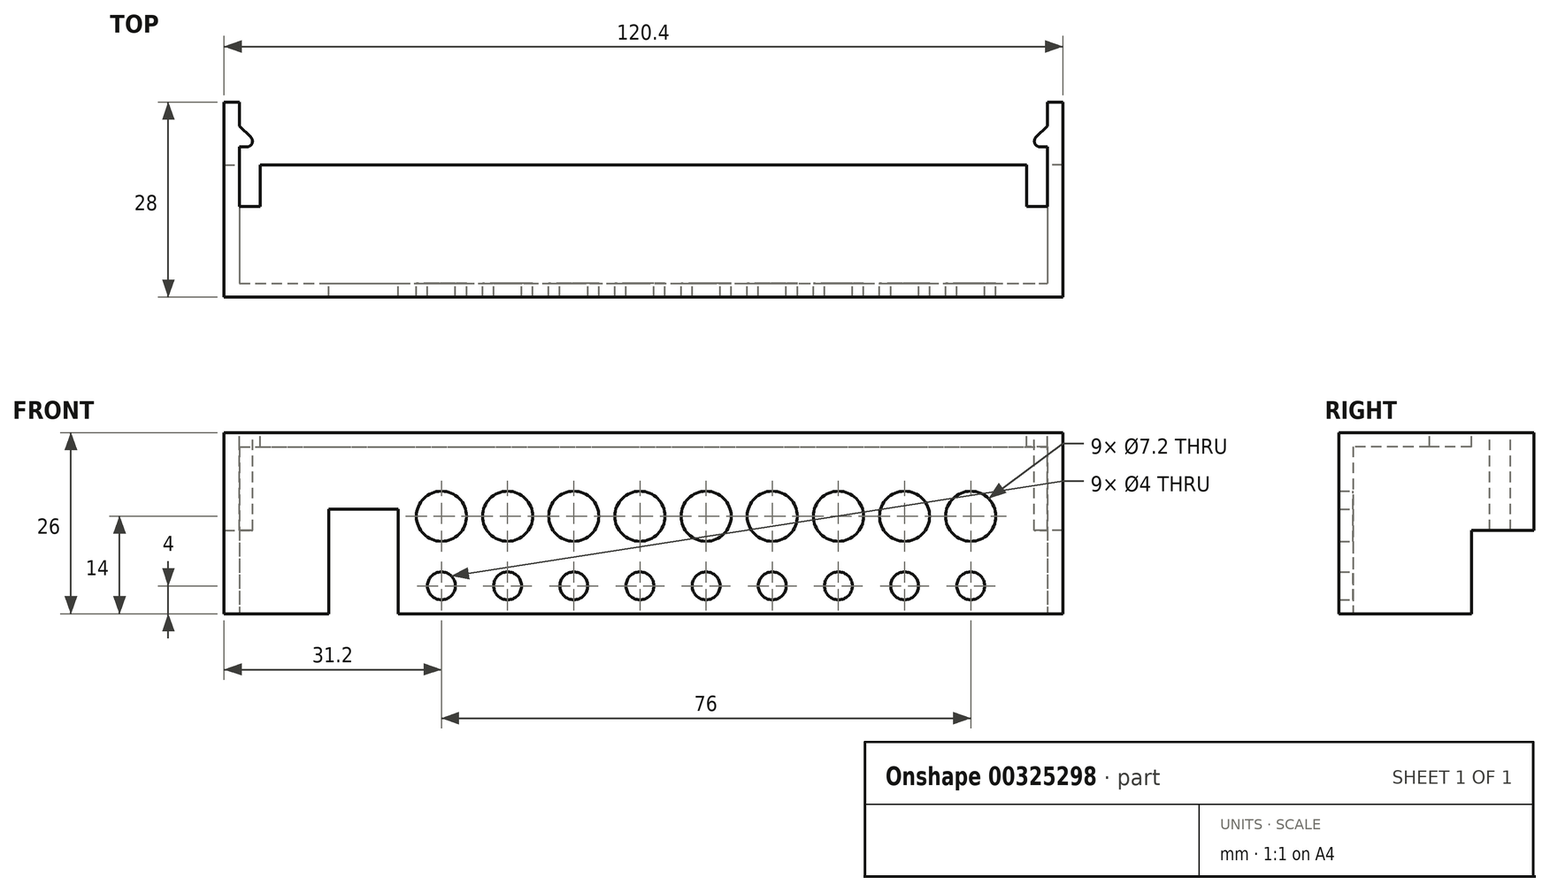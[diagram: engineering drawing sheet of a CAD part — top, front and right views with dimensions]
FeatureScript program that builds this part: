
annotation { "Feature Type Name" : "Feature", "Feature Type Description" : "" }
export const myFeature = defineFeature(function(context is Context, id is Id, definition is map)
    precondition{}
    {
        {
            var Q0;
            Q0=qCreatedBy(makeId("Top.planeOp"),FACE);
            var sketch = newSketch(context, id + "F0", { "sketchPlane" : qUnion([Q0])});
            skLineSegment(sketch, "E0.bottom", {"start": v(-58, 17) * mm, "end": v(58, 17) * mm});
            skLineSegment(sketch, "E0.top", {"start": v(-58, 0) * mm, "end": v(58, 0) * mm});
            skLineSegment(sketch, "E0.left", {"start": v(-58, 17) * mm, "end": v(-58, 0) * mm});
            skLineSegment(sketch, "E0.right", {"start": v(58, 17) * mm, "end": v(58, 0) * mm});
            skSolve(sketch);
        }
        {
            var Q0;
            Q0=makeQuery(id+"F0.imprint","IMPRINT",FACE,{"disambiguationData":[TD([[makeQuery(id+"F0.imprint","IMPRINT",EDGE,{"derivedFrom":sQuery(id+"F0.wireOp",EDGE,"E0.bottom")}),-1.0]])]});
            extrude(context, id + "F1", {"entities" : qUnion([Q0]), "depth" : 2 * mm});
        }
        {
            var Q0;
            Q0=makeQuery(id+"F1.opExtrude","SWEPT_FACE",FACE,{"disambiguationData":[OSD([sQuery(id+"F0.wireOp",EDGE,"E0.left")])]});
            var sketch = newSketch(context, id + "F2", { "sketchPlane" : qUnion([Q0])});
            skLineSegment(sketch, "E1.bottom", {"start": v(-17, 2) * mm, "end": v(0, 2) * mm});
            skLineSegment(sketch, "E1.top", {"start": v(-17, -24) * mm, "end": v(0, -24) * mm});
            skLineSegment(sketch, "E1.left", {"start": v(-17, 2) * mm, "end": v(-17, -24) * mm});
            skLineSegment(sketch, "E1.right", {"start": v(0, 2) * mm, "end": v(0, -24) * mm});
            skLineSegment(sketch, "E2.bottom", {"start": v(-17, -12) * mm, "end": v(-26, -12) * mm});
            skLineSegment(sketch, "E2.top", {"start": v(-17, 2) * mm, "end": v(-26, 2) * mm});
            skLineSegment(sketch, "E2.left", {"start": v(-17, -12) * mm, "end": v(-17, 2) * mm});
            skLineSegment(sketch, "E2.right", {"start": v(-26, -12) * mm, "end": v(-26, 2) * mm});
            skSolve(sketch);
        }
        {
            var Q0;
            {var subQ3=sQuery(id+"F2.wireOp",EDGE,"E2.bottom");Q0=makeQuery(id+"F2.imprint","IMPRINT",FACE,{"disambiguationData":[TD([[makeQuery(id+"F2.imprint","IMPRINT",EDGE,{"derivedFrom":subQ3}),-1.0]])]});}
            var Q1;
            {var subQ0=sQuery(id+"F2.wireOp",EDGE,"E1.bottom");Q1=makeQuery(id+"F2.imprint","IMPRINT",FACE,{"disambiguationData":[TD([[makeQuery(id+"F2.imprint","IMPRINT",EDGE,{"derivedFrom":subQ0}),-1.0]])]});}
            var Q2;
            {var subQ2=sQuery(id+"F2.wireOp",EDGE,"E1.top");Q2=makeQuery(id+"F2.imprint","IMPRINT",FACE,{"disambiguationData":[TD([[makeQuery(id+"F2.imprint","IMPRINT",EDGE,{"derivedFrom":subQ2}),1.0]])]});}
            extrude(context, id + "F3", {"entities" : qUnion([Q0, Q1, Q2]), "depth" : 2.2 * mm});
        }
        {
            var Q0;
            Q0=makeQuery(id+"F3.opExtrude","SWEPT_BODY",BODY,{"disambiguationData":[OSD([sQuery(id+"F2.wireOp",EDGE,"E1.bottom"),sQuery(id+"F2.wireOp",EDGE,"E1.top"),sQuery(id+"F2.wireOp",EDGE,"E1.left"),sQuery(id+"F2.wireOp",EDGE,"E1.right"),sQuery(id+"F2.wireOp",EDGE,"E2.bottom"),sQuery(id+"F2.wireOp",EDGE,"E2.top"),sQuery(id+"F2.wireOp",EDGE,"E2.right")])]});
            var Q1;
            Q1=qCreatedBy(makeId("Right.planeOp"),FACE);
            mirror(context, id + "F4", {"operationType" : NewBodyOperationType.ADD, "entities" : qUnion([Q0]), "mirrorPlane" : qUnion([Q1])});
        }
        {
            var Q0;
            {var subQ0=makeQuery(id+"F3.opExtrude","SWEPT_FACE",FACE,{"disambiguationData":[OSD([sQuery(id+"F2.wireOp",EDGE,"E1.bottom"),sQuery(id+"F2.wireOp",EDGE,"E2.top")])]});Q0=makeQuery(id+"F4.boolean.opBoolean","MERGE",FACE,{"derivedFrom":[makeQuery(id+"F1.opExtrude","CAP_FACE",FACE,{"disambiguationData":[OSD([sQuery(id+"F0.wireOp",EDGE,"E0.bottom"),sQuery(id+"F0.wireOp",EDGE,"E0.top"),sQuery(id+"F0.wireOp",EDGE,"E0.left"),sQuery(id+"F0.wireOp",EDGE,"E0.right")])],"isStart":false}),subQ0,makeQuery(id+"F4.opPattern","COPY",FACE,{"derivedFrom":subQ0,"instanceName":"1"})]});}
            var sketch = newSketch(context, id + "F5", { "sketchPlane" : qUnion([Q0])});
            skLineSegment(sketch, "E3.bottom", {"start": v(-58, 17) * mm, "end": v(-55, 17) * mm});
            skLineSegment(sketch, "E3.top", {"start": v(-58, 11) * mm, "end": v(-55, 11) * mm});
            skLineSegment(sketch, "E3.left", {"start": v(-58, 17) * mm, "end": v(-58, 11) * mm});
            skLineSegment(sketch, "E3.right", {"start": v(-55, 17) * mm, "end": v(-55, 11) * mm});
            skLineSegment(sketch, "E4.MirrorCS", {"start": v(58, 17) * mm, "end": v(55, 17) * mm});
            skLineSegment(sketch, "E5.MirrorCS", {"start": v(58, 17) * mm, "end": v(58, 11) * mm});
            skLineSegment(sketch, "E6.MirrorCS", {"start": v(58, 11) * mm, "end": v(55, 11) * mm});
            skLineSegment(sketch, "E7.MirrorCS", {"start": v(55, 17) * mm, "end": v(55, 11) * mm});
            skSolve(sketch);
        }
        {
            var Q0;
            Q0=makeQuery(id+"F5.imprint","IMPRINT",FACE,{"disambiguationData":[TD([[makeQuery(id+"F5.imprint","IMPRINT",EDGE,{"derivedFrom":sQuery(id+"F5.wireOp",EDGE,"E3.bottom")}),-1.0]])]});
            var Q1;
            Q1=makeQuery(id+"F5.imprint","IMPRINT",FACE,{"disambiguationData":[TD([[makeQuery(id+"F5.imprint","IMPRINT",EDGE,{"derivedFrom":sQuery(id+"F5.wireOp",EDGE,"E4.MirrorCS")}),-1.0]])]});
            extrude(context, id + "F6", {"entities" : qUnion([Q0, Q1]), "operationType" : NewBodyOperationType.REMOVE, "oppositeDirection" : true, "depth" : 25 * mm});
        }
        {
            var Q0;
            {var subQ0=makeQuery(id+"F3.opExtrude","SWEPT_FACE",FACE,{"disambiguationData":[OSD([sQuery(id+"F2.wireOp",EDGE,"E1.bottom"),sQuery(id+"F2.wireOp",EDGE,"E2.top")])]});Q0=makeQuery(id+"F4.boolean.opBoolean","MERGE",FACE,{"derivedFrom":[makeQuery(id+"F1.opExtrude","CAP_FACE",FACE,{"disambiguationData":[OSD([sQuery(id+"F0.wireOp",EDGE,"E0.bottom"),sQuery(id+"F0.wireOp",EDGE,"E0.top"),sQuery(id+"F0.wireOp",EDGE,"E0.left"),sQuery(id+"F0.wireOp",EDGE,"E0.right")])],"isStart":false}),subQ0,makeQuery(id+"F4.opPattern","COPY",FACE,{"derivedFrom":subQ0,"instanceName":"1"})]});}
            var sketch = newSketch(context, id + "F7", { "sketchPlane" : qUnion([Q0])});
            skLineSegment(sketch, "E8", {"start": v(-58, 22.6) * mm, "end": v(-55, 19.6) * mm});
            skLineSegment(sketch, "E9", {"start": v(-55, 19.6) * mm, "end": v(-58, 19.6) * mm});
            skLineSegment(sketch, "E10.0", {"start": v(-58, 11) * mm, "end": v(-58, 26) * mm});
            skLineSegment(sketch, "E11.MirrorCS", {"start": v(55, 19.6) * mm, "end": v(58, 19.6) * mm});
            skLineSegment(sketch, "E12.MirrorCS", {"start": v(58, 22.6) * mm, "end": v(55, 19.6) * mm});
            skLineSegment(sketch, "E13.MirrorCS", {"start": v(58, 11) * mm, "end": v(58, 26) * mm});
            skSolve(sketch);
        }
        {
            var Q0;
            {var subQ0=sQuery(id+"F7.wireOp",EDGE,"E8");Q0=makeQuery(id+"F7.imprint","IMPRINT",FACE,{"disambiguationData":[TD([[makeQuery(id+"F7.imprint","IMPRINT",EDGE,{"derivedFrom":subQ0}),-1.0]])]});}
            var Q1;
            {var subQ0=sQuery(id+"F7.wireOp",EDGE,"E11.MirrorCS");Q1=makeQuery(id+"F7.imprint","IMPRINT",FACE,{"disambiguationData":[TD([[makeQuery(id+"F7.imprint","IMPRINT",EDGE,{"derivedFrom":subQ0}),1.0]])]});}
            var Q2;
            Q2=makeQuery(id+"F3.opExtrude","SWEPT_FACE",FACE,{"disambiguationData":[OSD([sQuery(id+"F2.wireOp",EDGE,"E2.bottom")])]});
            extrude(context, id + "F8", {"entities" : qUnion([Q0, Q1]), "operationType" : NewBodyOperationType.ADD, "endBound" : BoundingType.UP_TO_SURFACE, "oppositeDirection" : true, "endBoundEntityFace" : qUnion([Q2]), "depth" : 25 * mm});
        }
        {
            var Q0;
            Q0=makeQuery(id+"F8.opExtrude","SWEPT_EDGE",EDGE,{"disambiguationData":[OSD([sQuery(id+"F7.wireOp",EDGE,"E11.MirrorCS"),sQuery(id+"F7.wireOp",EDGE,"E12.MirrorCS")])]});
            var Q1;
            Q1=makeQuery(id+"F8.opExtrude","SWEPT_EDGE",EDGE,{"disambiguationData":[OSD([sQuery(id+"F7.wireOp",EDGE,"E8"),sQuery(id+"F7.wireOp",EDGE,"E9")])]});
            var Q2;
            Q2=makeQuery(id+"F8.opExtrude","SWEPT_EDGE",EDGE,{"disambiguationData":[OSD([sQuery(id+"F7.wireOp",EDGE,"E11.MirrorCS"),sQuery(id+"F7.wireOp",EDGE,"E13.MirrorCS")])]});
            var Q3;
            Q3=makeQuery(id+"F8.opExtrude","SWEPT_EDGE",EDGE,{"disambiguationData":[OSD([sQuery(id+"F7.wireOp",EDGE,"E9"),sQuery(id+"F7.wireOp",EDGE,"E10.0")])]});
            var Q4;
            Q4=makeQuery(id+"F8.opExtrude","SWEPT_EDGE",EDGE,{"disambiguationData":[OSD([sQuery(id+"F7.wireOp",EDGE,"E8"),sQuery(id+"F7.wireOp",EDGE,"E10.0")])]});
            var Q5;
            Q5=makeQuery(id+"F8.opExtrude","SWEPT_EDGE",EDGE,{"disambiguationData":[OSD([sQuery(id+"F7.wireOp",EDGE,"E12.MirrorCS"),sQuery(id+"F7.wireOp",EDGE,"E13.MirrorCS")])]});
            fillet(context, id + "F9", {"entities" : qUnion([Q0, Q1, Q2, Q3, Q4, Q5]), "radius" : .8 * mm, "tangentPropagation" : true, "allowEdgeOverflow" : false});
        }
        {
            var Q0;
            {var subQ0=makeQuery(id+"F3.opExtrude","SWEPT_FACE",FACE,{"disambiguationData":[OSD([sQuery(id+"F2.wireOp",EDGE,"E1.right")])]});Q0=makeQuery(id+"F4.boolean.opBoolean","MERGE",FACE,{"derivedFrom":[makeQuery(id+"F1.opExtrude","SWEPT_FACE",FACE,{"disambiguationData":[OSD([sQuery(id+"F0.wireOp",EDGE,"E0.top")])]}),subQ0,makeQuery(id+"F4.opPattern","COPY",FACE,{"derivedFrom":subQ0,"instanceName":"1"})]});}
            var sketch = newSketch(context, id + "F10", { "sketchPlane" : qUnion([Q0])});
            skLineSegment(sketch, "E14.0", {"start": v(-60.2, 2) * mm, "end": v(-60.2, -24) * mm});
            skLineSegment(sketch, "E15.0", {"start": v(-60.2, 2) * mm, "end": v(60.2, 2) * mm});
            skLineSegment(sketch, "E16.0", {"start": v(60.2, 2) * mm, "end": v(60.2, -24) * mm});
            skLineSegment(sketch, "E17", {"start": v(-60.2, -24) * mm, "end": v(-45.2, -24) * mm});
            skLineSegment(sketch, "E18", {"start": v(-45.2, -24) * mm, "end": v(-45.2, -9) * mm});
            skLineSegment(sketch, "E19", {"start": v(-45.2, -9) * mm, "end": v(-35.2, -9) * mm});
            skLineSegment(sketch, "E20", {"start": v(-35.2, -9) * mm, "end": v(-35.2, -24) * mm});
            skLineSegment(sketch, "E21", {"start": v(-35.2, -24) * mm, "end": v(60.2, -24) * mm});
            skCircle(sketch, "E22", {"center": v(-29, -20) * mm, "radius": 2 * mm});
            skCircle(sketch, "E23", {"center": v(-29, -10) * mm, "radius": 3.6 * mm});
            skCircle(sketch, "E24.1.0.0", {"center": v(-19.5, -10) * mm, "radius": 3.6 * mm});
            skCircle(sketch, "E24.1.0.1", {"center": v(-19.5, -20) * mm, "radius": 2 * mm});
            skCircle(sketch, "E24.2.0.0", {"center": v(-10, -10) * mm, "radius": 3.6 * mm});
            skCircle(sketch, "E24.2.0.1", {"center": v(-10, -20) * mm, "radius": 2 * mm});
            skCircle(sketch, "E24.3.0.0", {"center": v(-0.5, -10) * mm, "radius": 3.6 * mm});
            skCircle(sketch, "E24.3.0.1", {"center": v(-0.5, -20) * mm, "radius": 2 * mm});
            skCircle(sketch, "E24.4.0.0", {"center": v(9, -10) * mm, "radius": 3.6 * mm});
            skCircle(sketch, "E24.4.0.1", {"center": v(9, -20) * mm, "radius": 2 * mm});
            skCircle(sketch, "E24.5.0.0", {"center": v(18.5, -10) * mm, "radius": 3.6 * mm});
            skCircle(sketch, "E24.5.0.1", {"center": v(18.5, -20) * mm, "radius": 2 * mm});
            skCircle(sketch, "E24.6.0.0", {"center": v(28, -10) * mm, "radius": 3.6 * mm});
            skCircle(sketch, "E24.6.0.1", {"center": v(28, -20) * mm, "radius": 2 * mm});
            skCircle(sketch, "E24.7.0.0", {"center": v(37.5, -10) * mm, "radius": 3.6 * mm});
            skCircle(sketch, "E24.7.0.1", {"center": v(37.5, -20) * mm, "radius": 2 * mm});
            skCircle(sketch, "E24.8.0.0", {"center": v(47, -10) * mm, "radius": 3.6 * mm});
            skCircle(sketch, "E24.8.0.1", {"center": v(47, -20) * mm, "radius": 2 * mm});
            skLineSegment(sketch, "E24.direction1", {"start": v(-29, -10) * mm, "end": v(-19.5, -10) * mm, "construction": true});
            skSolve(sketch);
        }
        {
            var Q0;
            {var subQ1=sQuery(id+"F10.wireOp",EDGE,"E18");Q0=makeQuery(id+"F10.imprint","IMPRINT",FACE,{"disambiguationData":[TD([[makeQuery(id+"F10.imprint","IMPRINT",EDGE,{"derivedFrom":subQ1}),1.0]])]});}
            var Q1;
            {var subQ3=sQuery(id+"F10.wireOp",EDGE,"E14.0");Q1=makeQuery(id+"F10.imprint","IMPRINT",FACE,{"disambiguationData":[TD([[makeQuery(id+"F10.imprint","IMPRINT",EDGE,{"derivedFrom":subQ3}),1.0]])]});}
            extrude(context, id + "F11", {"entities" : qUnion([Q0, Q1]), "operationType" : NewBodyOperationType.ADD, "depth" : 2 * mm});
        }
    });
